# Revit family: AFX-Studio-Flush_Mount-1
name_source: partatom
category: Lighting Fixtures
units: mm (PartAtom-declared; Revit-internal decimal feet)

## family parameters
Cut with Voids When Loaded = No
Host = Face
Light Source = Yes
Part Type = Normal
Room Calculation Point = No
Round Connector Dimension = Use Diameter
Shared = No

## types (2) — shared parameters
Apparent Load = 0 VA
Assembly Code = D5020200
Canopy Finish = AFX - Black Steel
Color Filter = 16777215
Colour Rendering Index = 90
Connector Finish = AFX - Black Steel
Default Elevation = 48"
Depth = 3 1/4"
Diffuser Finish = AFX - White Acrylic
Dimming Lamp Color Temperature Shift = <None>
Emit Shape Visible in Rendering = No
Keynote = 12500
Lamp = LED
Manufacturer = AFX Inc
Power Factor = 1
Product Documentation Link = https://www.afxinc.com
Screen Finish = AFX - White Acrylic
Tilt Angle = -90.00°
Type Comments = Studio
URL = https://www.afxinc.com
Voltage = 120 V

## per-type parameters (varying)
| type | 12inch | 16inch | Description | Diameter | Distance Connector | Emit from Circle Diameter | Photometric Web File | Wattage Comments |
| STDF12LAJD1BK | Yes | No | LED Flush Mount - 12"Dia x 3 1/4"D | 12" | 2 5/32" | 11" | STDF12LAJD1SB_3000K.IES | 20 |
| STDF16LAJD1BK | No | Yes | LED Flush Mount - 15 1/2"Dia x 3 1/4"D | 15 1/2" | 3 29/32" | 14 1/2" | STDF16LAJD1PC_3000K.IES | 25 |

note: column(s) folded — value = type name in every type: Model

## geometry (parser evidence)
native form markers: Sweep x6
no freeform markers — native parametric forms only
